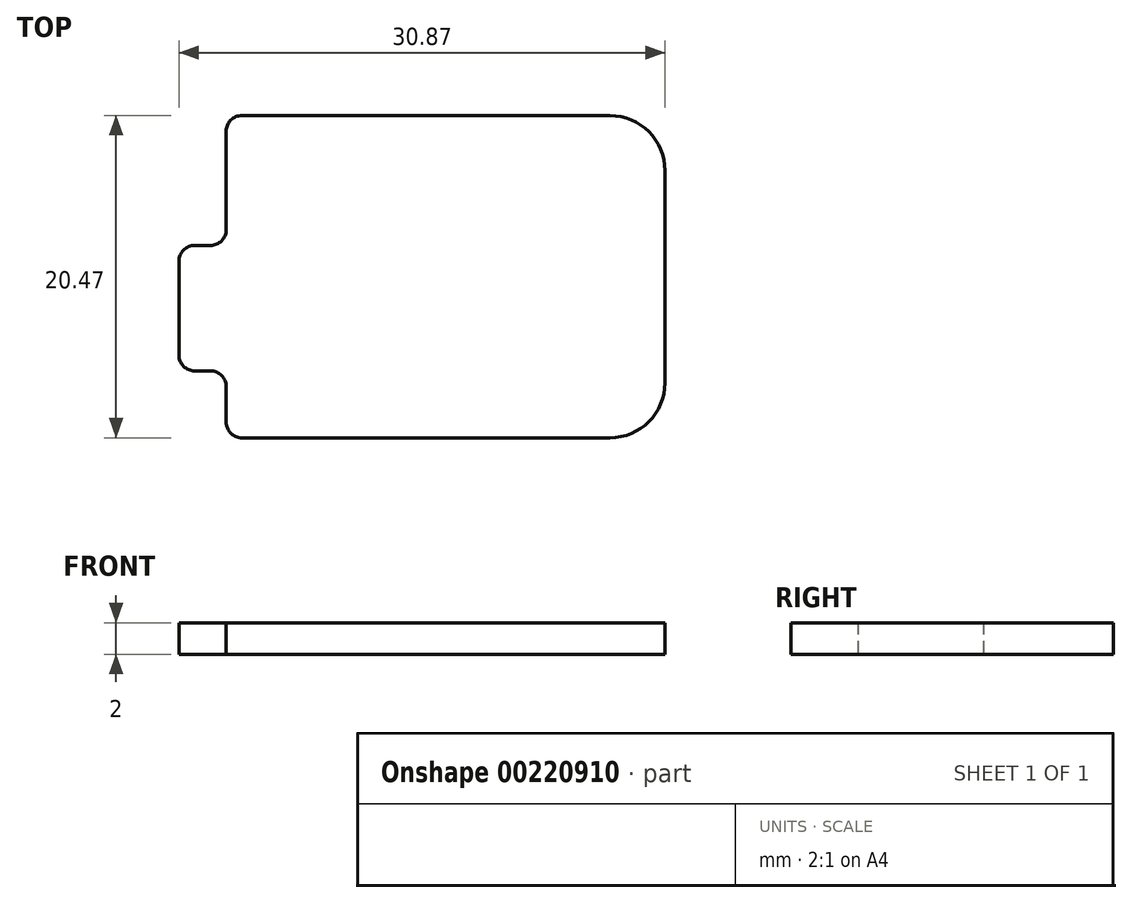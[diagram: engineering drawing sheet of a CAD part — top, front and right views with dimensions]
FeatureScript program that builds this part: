
annotation { "Feature Type Name" : "Feature", "Feature Type Description" : "" }
export const myFeature = defineFeature(function(context is Context, id is Id, definition is map)
    precondition{}
    {
        {
            var Q0;
            Q0=qCreatedBy(makeId("Top.planeOp"),FACE);
            var sketch = newSketch(context, id + "F0", { "sketchPlane" : qUnion([Q0])});
            skLineSegment(sketch, "E0.bottom", {"start": v(-26.87, 20.47) * mm, "end": v(-3.5, 20.47) * mm});
            skLineSegment(sketch, "E0.top", {"start": v(-26.87, 0) * mm, "end": v(-3.5, 0) * mm});
            skLineSegment(sketch, "E0.left", {"start": v(-30.87, 11.22) * mm, "end": v(-30.87, 5.25) * mm});
            skLineSegment(sketch, "E0.right", {"start": v(0, 16.97) * mm, "end": v(0, 3.5) * mm});
            skPoint(sketch, "E0.middle", {"position": v(0, 0) * mm});
            skLineSegment(sketch, "E1", {"start": v(-27.87, 19.47) * mm, "end": v(-27.87, 13.22) * mm});
            skLineSegment(sketch, "E2", {"start": v(-28.87, 12.22) * mm, "end": v(-29.87, 12.22) * mm});
            skLineSegment(sketch, "E3", {"start": v(-29.87, 4.25) * mm, "end": v(-28.87, 4.25) * mm});
            skLineSegment(sketch, "E4", {"start": v(-27.87, 3.25) * mm, "end": v(-27.87, 1) * mm});
            skPoint(sketch, "E5.visualSharp", {"position": v(0, 20.47) * mm});
            skArc(sketch, "E5.filletArc", {"start": v(0, 16.97) * mm, "mid": v(-1.03, 19.44) * mm, "end": v(-3.5, 20.47) * mm});
            skArc(sketch, "E6.filletArc", {"start": v(-3.5, 0) * mm, "mid": v(-1.03, 1.03) * mm, "end": v(0, 3.5) * mm});
            skPoint(sketch, "E7.visualSharp", {"position": v(-27.87, 0) * mm});
            skArc(sketch, "E7.filletArc", {"start": v(-27.87, 1) * mm, "mid": v(-27.58, 0.3) * mm, "end": v(-26.87, 0) * mm});
            skPoint(sketch, "E8.visualSharp", {"position": v(-27.87, 20.47) * mm});
            skArc(sketch, "E8.filletArc", {"start": v(-26.87, 20.47) * mm, "mid": v(-27.58, 20.18) * mm, "end": v(-27.87, 19.47) * mm});
            skPoint(sketch, "E9.visualSharp", {"position": v(-30.87, 12.22) * mm});
            skArc(sketch, "E9.filletArc", {"start": v(-29.87, 12.22) * mm, "mid": v(-30.58, 11.93) * mm, "end": v(-30.87, 11.22) * mm});
            skPoint(sketch, "E10.visualSharp", {"position": v(-30.87, 4.25) * mm});
            skArc(sketch, "E10.filletArc", {"start": v(-30.87, 5.25) * mm, "mid": v(-30.58, 4.54) * mm, "end": v(-29.87, 4.25) * mm});
            skPoint(sketch, "E11.visualSharp", {"position": v(-27.87, 12.22) * mm});
            skArc(sketch, "E11.filletArc", {"start": v(-28.87, 12.22) * mm, "mid": v(-28.16, 12.51) * mm, "end": v(-27.87, 13.22) * mm});
            skPoint(sketch, "E12.visualSharp", {"position": v(-27.87, 4.25) * mm});
            skArc(sketch, "E12.filletArc", {"start": v(-27.87, 3.25) * mm, "mid": v(-28.16, 3.96) * mm, "end": v(-28.87, 4.25) * mm});
            skSolve(sketch);
        }
        {
            var Q0;
            Q0 = qSketchRegion(id + "F0", true);
            extrude(context, id + "F1", {"entities" : qUnion([Q0]), "depth" : 2 * mm});
        }
    });
